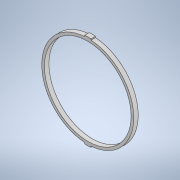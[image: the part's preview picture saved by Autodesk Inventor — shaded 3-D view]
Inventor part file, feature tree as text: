
AUTODESK INVENTOR PART (.ipt)
format: ipt  version: 2020.2 (Build 242310000, 310)  size: 117,760 bytes
history: native  units: mm
features: extrude x1, sketch x1
ambient origin geometry x8: Origin, YZ Plane, XZ Plane, XY Plane, X Axis, Y Axis, Z Axis, Center Point
bodies: Solid1 (feature_tree)
feature tree (2):
  extrude  "Extrusion1"  Depth=2.03mm
  sketch  "Sketch1"  dims[d0=41.8mm d1=1.2mm d2=0.5mm d3=0.5mm d4=2.87mm d5=2.03mm d6=0.0mm]
